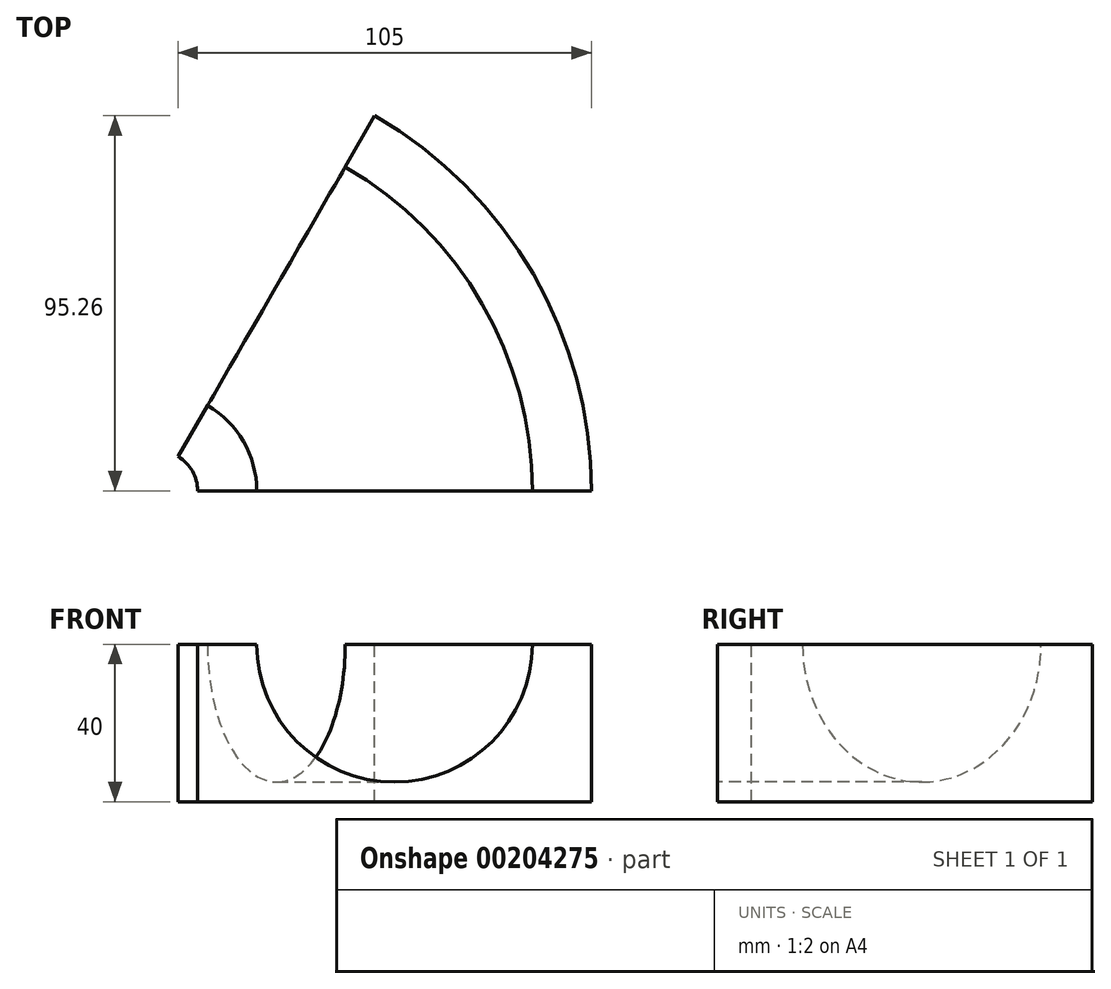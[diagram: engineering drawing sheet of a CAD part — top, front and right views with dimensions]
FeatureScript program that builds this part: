
annotation { "Feature Type Name" : "Feature", "Feature Type Description" : "" }
export const myFeature = defineFeature(function(context is Context, id is Id, definition is map)
    precondition{}
    {
        {
            var Q0;
            Q0=qCreatedBy(makeId("Front.planeOp"),FACE);
            var sketch = newSketch(context, id + "F0", { "sketchPlane" : qUnion([Q0])});
            skLineSegment(sketch, "E0.bottom", {"start": v(-50, -19.67) * mm, "end": v(0, -19.67) * mm});
            skLineSegment(sketch, "E0.top", {"start": v(-50, 20.33) * mm, "end": v(0, 20.33) * mm});
            skLineSegment(sketch, "E0.left", {"start": v(-50, -19.67) * mm, "end": v(-50, 20.33) * mm});
            skLineSegment(sketch, "E1.MirrorCS", {"start": v(50, -19.67) * mm, "end": v(0, -19.67) * mm});
            skLineSegment(sketch, "E2.MirrorCS", {"start": v(50, -19.67) * mm, "end": v(50, 20.33) * mm});
            skLineSegment(sketch, "E3.MirrorCS", {"start": v(50, 20.33) * mm, "end": v(0, 20.33) * mm});
            skArc(sketch, "E4", {"start": v(-35, 20.33) * mm, "mid": v(0, -14.67) * mm, "end": v(35, 20.33) * mm});
            skLineSegment(sketch, "E5.MirrorCS", {"start": v(-60, 20.33) * mm, "end": v(-60, -18.07) * mm, "construction": true});
            skSolve(sketch);
        }
        {
            var Q0;
            Q0=makeQuery(id+"F0.imprint","IMPRINT",FACE,{"disambiguationData":[TD([[makeQuery(id+"F0.imprint","IMPRINT",EDGE,{"derivedFrom":sQuery(id+"F0.wireOp",EDGE,"E0.bottom")}),1.0]])]});
            var Q1;
            Q1=sQuery(id+"F0.wireOp",EDGE,"E5.MirrorCS");
            revolve(context, id + "F1", {"entities" : qUnion([Q0]), "axis" : qUnion([Q1]), "revolveType" : RevolveType.ONE_DIRECTION, "oppositeDirection" : true, "angle" : 60 * degree});
        }
    });
